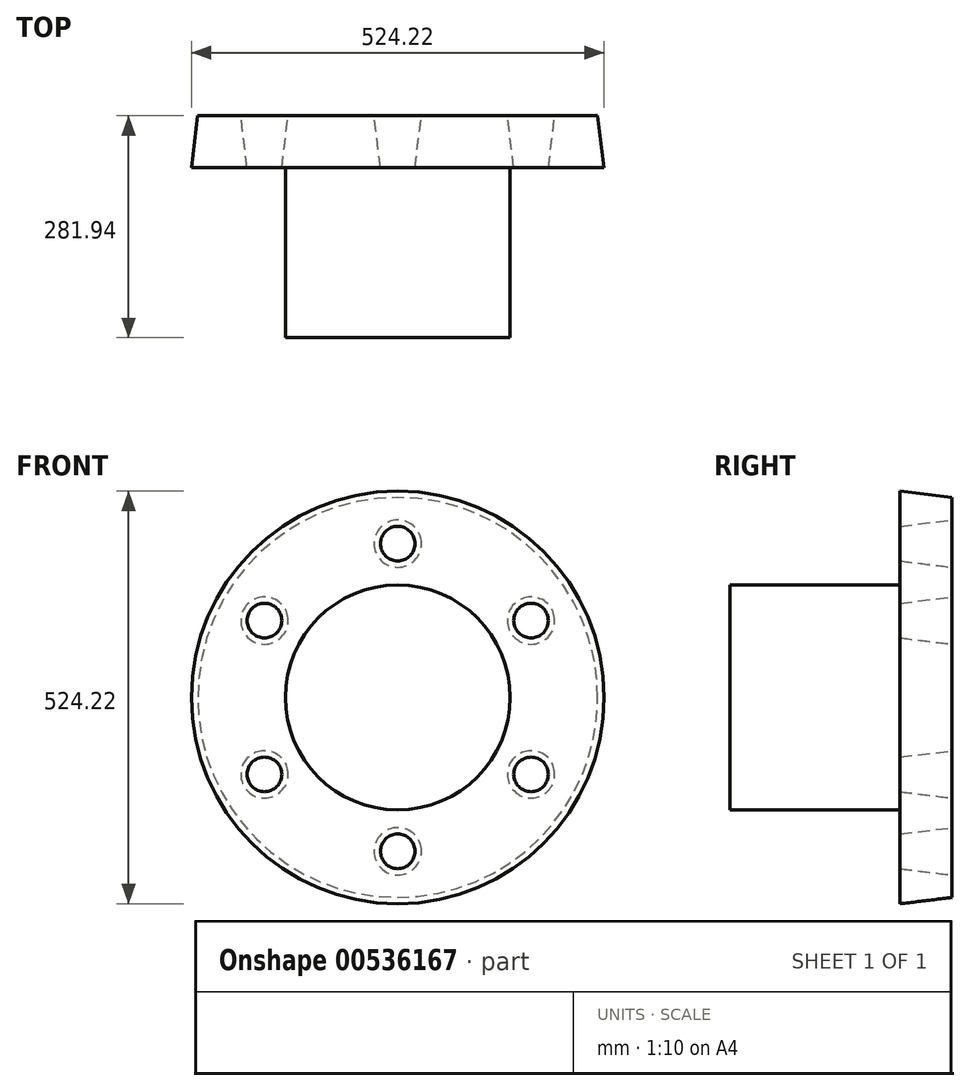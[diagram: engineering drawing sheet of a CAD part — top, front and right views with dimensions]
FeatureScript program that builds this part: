
annotation { "Feature Type Name" : "Feature", "Feature Type Description" : "" }
export const myFeature = defineFeature(function(context is Context, id is Id, definition is map)
    precondition{}
    {
        {
            var Q0;
            Q0=qCreatedBy(makeId("Front.planeOp"),FACE);
            var sketch = newSketch(context, id + "F0", { "sketchPlane" : qUnion([Q0])});
            skCircle(sketch, "E0", {"center": v(0, 0) * mm, "radius": 254 * mm});
            skCircle(sketch, "E1", {"center": v(0, 195.47) * mm, "radius": 30.08 * mm});
            skCircle(sketch, "E2.1.0", {"center": v(-169.28, 97.73) * mm, "radius": 30.08 * mm});
            skCircle(sketch, "E2.2.0", {"center": v(-169.28, -97.73) * mm, "radius": 30.08 * mm});
            skCircle(sketch, "E2.3.0", {"center": v(0, -195.47) * mm, "radius": 30.08 * mm});
            skCircle(sketch, "E2.4.0", {"center": v(169.28, -97.73) * mm, "radius": 30.08 * mm});
            skCircle(sketch, "E2.5.0", {"center": v(169.28, 97.73) * mm, "radius": 30.08 * mm});
            skSolve(sketch);
        }
        {
            var Q0;
            Q0=makeQuery(id+"F0.imprint","IMPRINT",FACE,{"disambiguationData":[TD([[makeQuery(id+"F0.imprint","IMPRINT",EDGE,{"derivedFrom":sQuery(id+"F0.wireOp",EDGE,"E0")}),1.0]])]});
            extrude(context, id + "F1", {"entities" : qUnion([Q0]), "depth" : 66.04 * mm, "offsetDistance" : 25.4 * mm, "hasDraft" : true, "draftAngle" : 7 * degree});
        }
        {
            var Q0;
            Q0=makeQuery(id+"F1.opExtrude","CAP_FACE",FACE,{"disambiguationData":[OSD([sQuery(id+"F0.wireOp",EDGE,"E0"),sQuery(id+"F0.wireOp",EDGE,"E1"),sQuery(id+"F0.wireOp",EDGE,"E2.1.0"),sQuery(id+"F0.wireOp",EDGE,"E2.2.0"),sQuery(id+"F0.wireOp",EDGE,"E2.3.0"),sQuery(id+"F0.wireOp",EDGE,"E2.4.0"),sQuery(id+"F0.wireOp",EDGE,"E2.5.0")])],"isStart":false});
            var sketch = newSketch(context, id + "F2", { "sketchPlane" : qUnion([Q0])});
            skCircle(sketch, "E3", {"center": v(0, 0) * mm, "radius": 142.83 * mm});
            skSolve(sketch);
        }
        {
            var Q0;
            Q0 = qSketchRegion(id + "F2", true);
            extrude(context, id + "F3", {"entities" : qUnion([Q0]), "operationType" : NewBodyOperationType.ADD, "depth" : 215.9 * mm, "offsetDistance" : 25.4 * mm});
        }
    });
